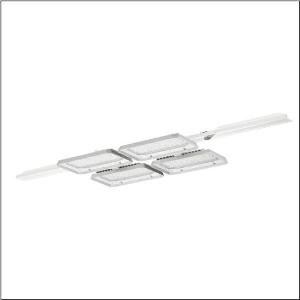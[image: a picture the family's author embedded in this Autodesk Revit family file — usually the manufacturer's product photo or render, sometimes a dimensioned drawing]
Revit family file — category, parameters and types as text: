
# Revit family: highbay_11_51hla1d24nla
name_source: partatom
category: Lighting Fixtures
units: mm (PartAtom-declared; Revit-internal decimal feet)

## family parameters
Cut with Voids When Loaded = No
Host = Face
Light Source = No
Part Type = Normal
Room Calculation Point = No
Round Connector Dimension = Use Diameter
Shared = No

## types (1)
- --- (1 x LED, 32370 lm, 189.7 W, 4000K)
    Apparent Load = 759 VA
    CIE Flux Codes = 88 95 99 100 99
    Color Rendering = 80
    Color Temperature = 4000K
    Default Elevation = 1800 mm
    Description = Highbay 11, LED high bay luminaire, end cap, primary light control with lens, of PMMA, light emission: direct distribution, primary light characteristic: symmetric, installation type: recessed, for 2x 2x LED, rated luminous flux: 32.370lm, luminous efficacy: 171lm/W, light colour: 840, colour temperature: 4000K, control gear: ECG DALI, with system connector, mains connection: 230..240V, AC, 50/60Hz, rated input power: 190W, LED unit, of diecast aluminium, unplated, bead blasted, silver, for tool-free mounting of luminaire to Licross® trunking rail, length: 1.500mm, width: 500mm, height: 65mm, housing, of diecast aluminium, uncoated, bead blasted, silver, fixing on rail side, of aluminium, anodised, metallic grey, end cap, of PC, grey, protection rating (complete): IP64, insulation class (complete): insulation class I (protective earthing), certification: CE, UKCA, protection symbol: D, impact resistance: IK08 with glass or PC cover, permissible operating ambient temperature: -35..+45°C, corresponds to IFS (International Featured Standards) requirements for safety and quality in the food industry, packaging unit: 1 piece
    Height = 105 mm
    Lamp = 1 x LED
    Lamp Light Flux = 32370 lm
    Lamp Power = 189.7 W
    Lamp count = 1
    Length = 1500 mm
    Luminous efficacy = 171 lm/W
    Manufacturer = Siteco
    ModVariant = No
    Model = 51HLA1D24NLA
    Mounting Place = Ceiling
    Mounting Type = Pendant
    Number of Poles = 1
    OnlyDefault = Yes
    Power Factor = 1
    Product Name = Highbay 11
    Product group = LED high bay luminaire
    ProductGroupID = 903
    Protection Class = Protection class I
    Protection Degree = IP 64
    RLX_Detail_Level = 1
    RLX_Emergency_Light_Flux = 0 lm
    RLX_Emergency_Type = 0
    RLX_Emergency_Type_DB = No
    RlxData = <blob elided: 87881 chars, md5=c1a76442>
    Socket = socket
    Standby Power = 0 W
    System Light Flux = 129480 lm
    System Power = 759 W
    Type Comments = factory setting: luminous flux: 100 % | dim-lin: 254 | 535 mA
    Type Image = l_1004707.jpg
    URL = http://relux.com
    VarID = @adj_158143
    Voltage = 0 V
    Weight = 0.00 kg
    Width = 500 mm

## geometry (parser evidence)
native form markers: Blend x4, Sweep x18
no freeform markers — native parametric forms only
